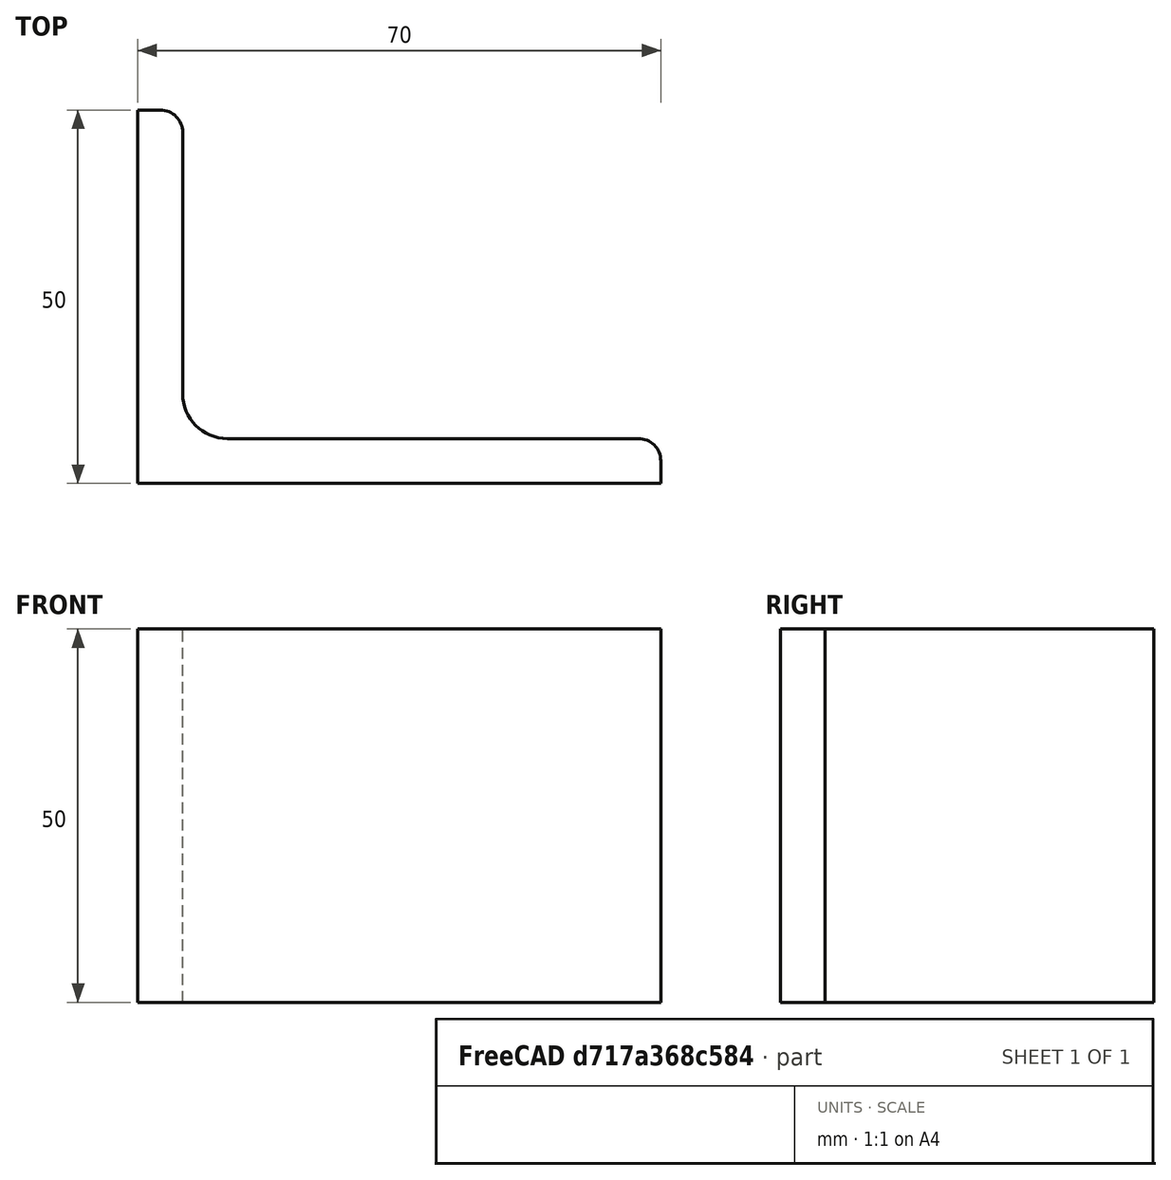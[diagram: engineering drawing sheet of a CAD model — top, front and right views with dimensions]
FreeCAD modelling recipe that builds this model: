
FCSTD DOCUMENT  (FreeCAD 0.15R4671 (Git))
Label: Angle Bar 70x50x6 EN10056 S235JR
License: All rights reserved
LicenseURL: http://en.wikipedia.org/wiki/All_rights_reserved
objects: Sketcher::SketchObject×1, Part::Extrusion×1
note: 2 computed .brp shape members not serialized (recipe doc carries the construction recipe); baked Part::Feature solids carry a one-line shape summary decoded from their .brp

FEATURE [Sketcher::SketchObject] Sketch
  sketch-geometry (9):
    g0: LineSegment StartX=0 StartY=0 StartZ=0 EndX=70 EndY=0 EndZ=0
    g1: LineSegment StartX=70 StartY=0 StartZ=0 EndX=70 EndY=3 EndZ=0
    g2: LineSegment StartX=67 StartY=6 StartZ=0 EndX=12 EndY=6 EndZ=0
    g3: LineSegment StartX=0 StartY=0 StartZ=0 EndX=0 EndY=50 EndZ=0
    g4: LineSegment StartX=0 StartY=50 StartZ=0 EndX=3 EndY=50 EndZ=0
    g5: LineSegment StartX=6 StartY=47 StartZ=0 EndX=6 EndY=12 EndZ=0
    g6: ArcOfCircle CenterX=12 CenterY=12 CenterZ=0 NormalX=0 NormalY=0 NormalZ=1 Radius=6 StartAngle=3.14159 EndAngle=4.71239
    g7: ArcOfCircle CenterX=3 CenterY=47 CenterZ=0 NormalX=0 NormalY=0 NormalZ=1 Radius=3 StartAngle=0 EndAngle=1.5708
    g8: ArcOfCircle CenterX=67 CenterY=3 CenterZ=0 NormalX=0 NormalY=0 NormalZ=1 Radius=3 StartAngle=0 EndAngle=1.5708
  constraints (23):
    c: Coincident(g0,g-1)
    c: Horizontal(g0)
    c: Coincident(g1,g0)
    c: Vertical(g1)
    c: Horizontal(g2)
    c: Coincident(g3,g-1)
    c: Vertical(g3)
    c: Coincident(g4,g3)
    c: Horizontal(g4)
    c: Vertical(g5)
    c: Tangent(g5,g6) = -1.5708
    c: Tangent(g2,g6) = 1.5708
    c: Tangent(g4,g7) = 1.5708
    c: Tangent(g5,g7) = 1.5708
    c: Tangent(g2,g8) = -1.5708
    c: Tangent(g1,g8) = -1.5708
    c: DistanceX(g0) = 70
    c: DistanceY(g3) = 50
    c: DistanceY(g0,g2) = 6
    c: DistanceX(g3,g5) = 6
    c: Radius(g6) = 6
    c: Radius(g8) = 3
    c: Radius(g7) = 3
FEATURE [Part::Extrusion] Extrude  label="Angle Bar 70x50x6 EN10056 S235JR"
  Base = -> Sketch
  Dir = (0,0,50)
  Solid = true
